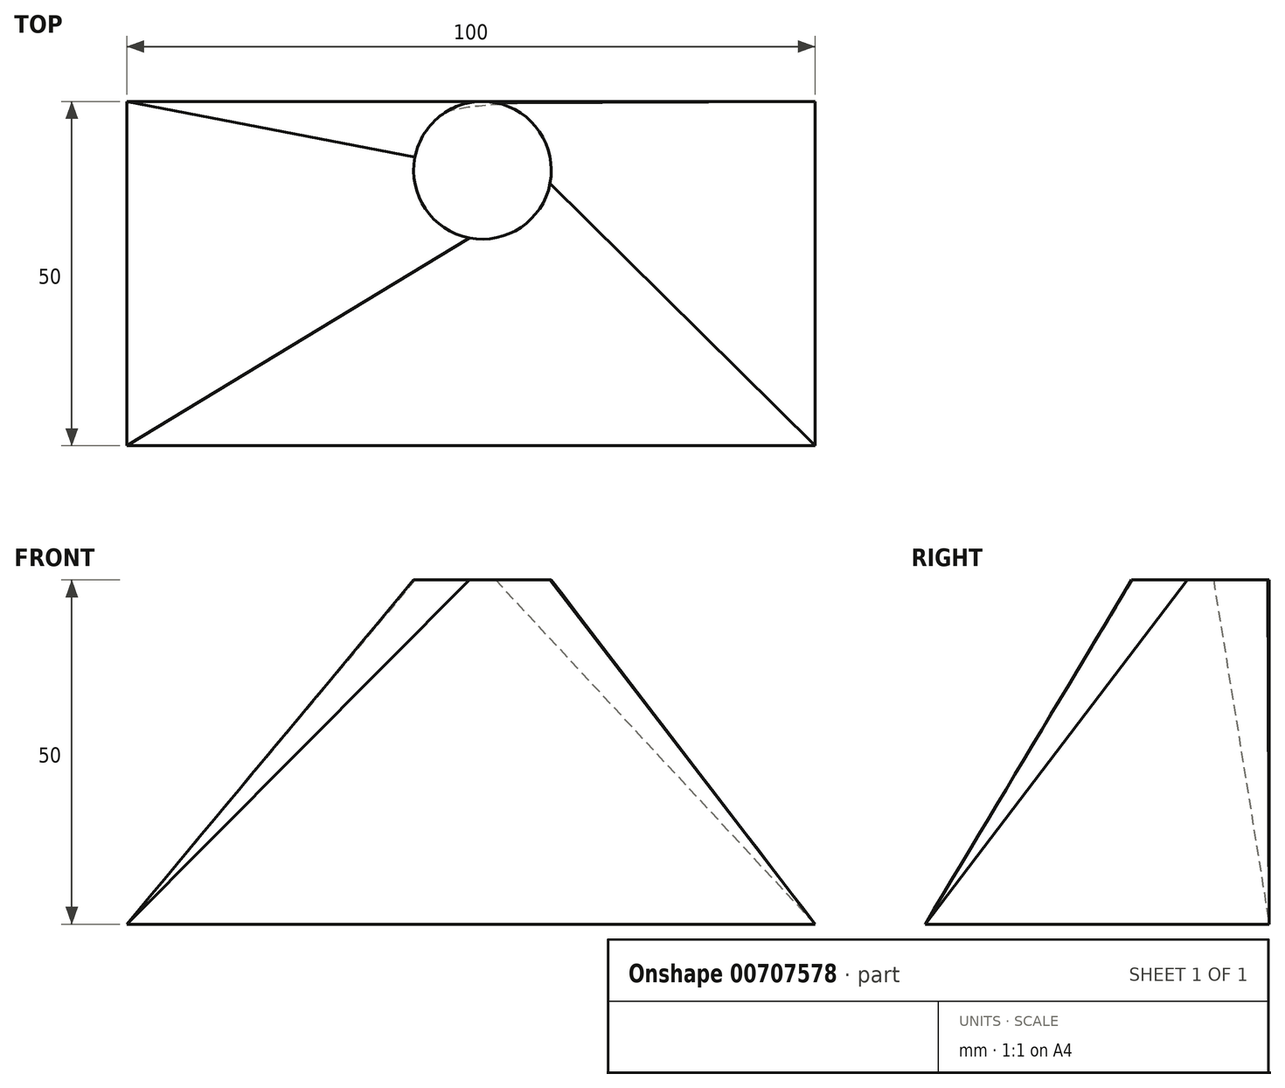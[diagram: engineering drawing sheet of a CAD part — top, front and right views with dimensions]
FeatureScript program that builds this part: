
annotation { "Feature Type Name" : "Feature", "Feature Type Description" : "" }
export const myFeature = defineFeature(function(context is Context, id is Id, definition is map)
    precondition{}
    {
        {
            var Q0;
            Q0=qCreatedBy(makeId("Top.planeOp"),FACE);
            var sketch = newSketch(context, id + "F0", { "sketchPlane" : qUnion([Q0])});
            skLineSegment(sketch, "E0.bottom", {"start": v(-51.67, 0) * mm, "end": v(48.33, 0) * mm});
            skLineSegment(sketch, "E0.top", {"start": v(-51.67, -50) * mm, "end": v(48.33, -50) * mm});
            skLineSegment(sketch, "E0.left", {"start": v(-51.67, 0) * mm, "end": v(-51.67, -50) * mm});
            skLineSegment(sketch, "E0.right", {"start": v(48.33, 0) * mm, "end": v(48.33, -50) * mm});
            skSolve(sketch);
        }
        {
            var Q0;
            Q0=qCreatedBy(makeId("Top.planeOp"),FACE);
            cPlane(context, id + "F1", {"entities" : qUnion([Q0]), "cplaneType" : CPlaneType.OFFSET, "offset" : 50 * mm, "width" : 150 * mm, "height" : 150 * mm});
        }
        {
            var Q0;
            Q0=qCreatedBy(id+"F1.planeOp",FACE);
            var sketch = newSketch(context, id + "F2", { "sketchPlane" : qUnion([Q0])});
            skCircle(sketch, "E1", {"center": v(0, -10) * mm, "radius": 10 * mm});
            skSolve(sketch);
        }
        {
            var Q0;
            Q0=makeQuery(id+"F2.imprint","IMPRINT",FACE,{"disambiguationData":[TD([[makeQuery(id+"F2.imprint","IMPRINT",EDGE,{"derivedFrom":sQuery(id+"F2.wireOp",EDGE,"E1")}),1.0]])]});
            var Q1;
            Q1=makeQuery(id+"F0.imprint","IMPRINT",FACE,{"disambiguationData":[TD([[makeQuery(id+"F0.imprint","IMPRINT",EDGE,{"derivedFrom":sQuery(id+"F0.wireOp",EDGE,"E0.bottom")}),-1.0]])]});
            loft(context, id + "F3", {"sheetProfilesArray" : [{ "sheetProfileEntities" : qUnion([Q0]) }, { "sheetProfileEntities" : qUnion([Q1]) }]});
        }
    });
